# Revit family: MINI INGROUND 12W SIMETRICA_EM12SW.145
name_source: partatom
category: Luminarias
units: mm (PartAtom-declared; Revit-internal decimal feet)

## family parameters
Compartido = No
Corte con vacíos al cargar = No
Cota de conector redondo = Diámetro de uso
Origen de luz = Sí
Punto de cálculo de habitación = No
Se basa en plano de trabajo = Sí
Siempre vertical = No
Tipo de pieza = Normal

## types (1)
- EMP_EM12SW.145
    Archivo de red fotométrica = EM12SW.1_45º.ies
    Cambio de temperatura de color de luz atenuada = <Ninguno>
    Comentarios de vataje = 100-240V
    Descripción = LUMINARIA TIPO CIRCULAR PARA EMPOTRAR EN PISO CON CUERPO DE ALUMINIO FUNDIDO A PRESION CUBIERTO CON POLVO GRIS OSCURO, CON CUBIERTA DE ACERO INOXIDABLE Y VIDRIO TEMPLADO DE 8MM, CON 173MM DE DIAMETRO Y 38MM DE PROFUNDIDAD, INSTALACION EMPOTRABLE EN PISO CON POCO ESPACIO, USO PARA INTERIORES COMO EXTERIORES CON IP 67, CUENTA CON 6 LED TIPO OSRAM CON UNA POTENCIA TOTAL DE 13.5W, A UNA TEMPERATURA EN BLANCO CALIDO 3000K CON 783 LUMENES, 111mA EN CORRIENTE DE OPERACIÓN, IK08, IRC 80, DISPONIBLE PARA ATENUAR EN TRIAC, APERTURA A 45 GRADOS POR PROYECTO, FUENTE REMOTA (INCLUIDA) CON 56MM DE ANCHO, ALIMENTADA A 100-240V.
    Elevación por defecto = 0 mm  [stored 0 ft]
    Fabricante = BRILLANT
    Filtro de color = 16777215
    Lámpara = OSRAM
    Modelo = EM12SW.145
    Watt per fixture = 13.5
    Ángulo de inclinación = 45.00°

note: [stored X ft] marks values corroborated as IEEE doubles in the binary element streams (Revit-internal decimal feet)

## geometry (parser evidence)
native form markers: Blend x2
no freeform markers — native parametric forms only
